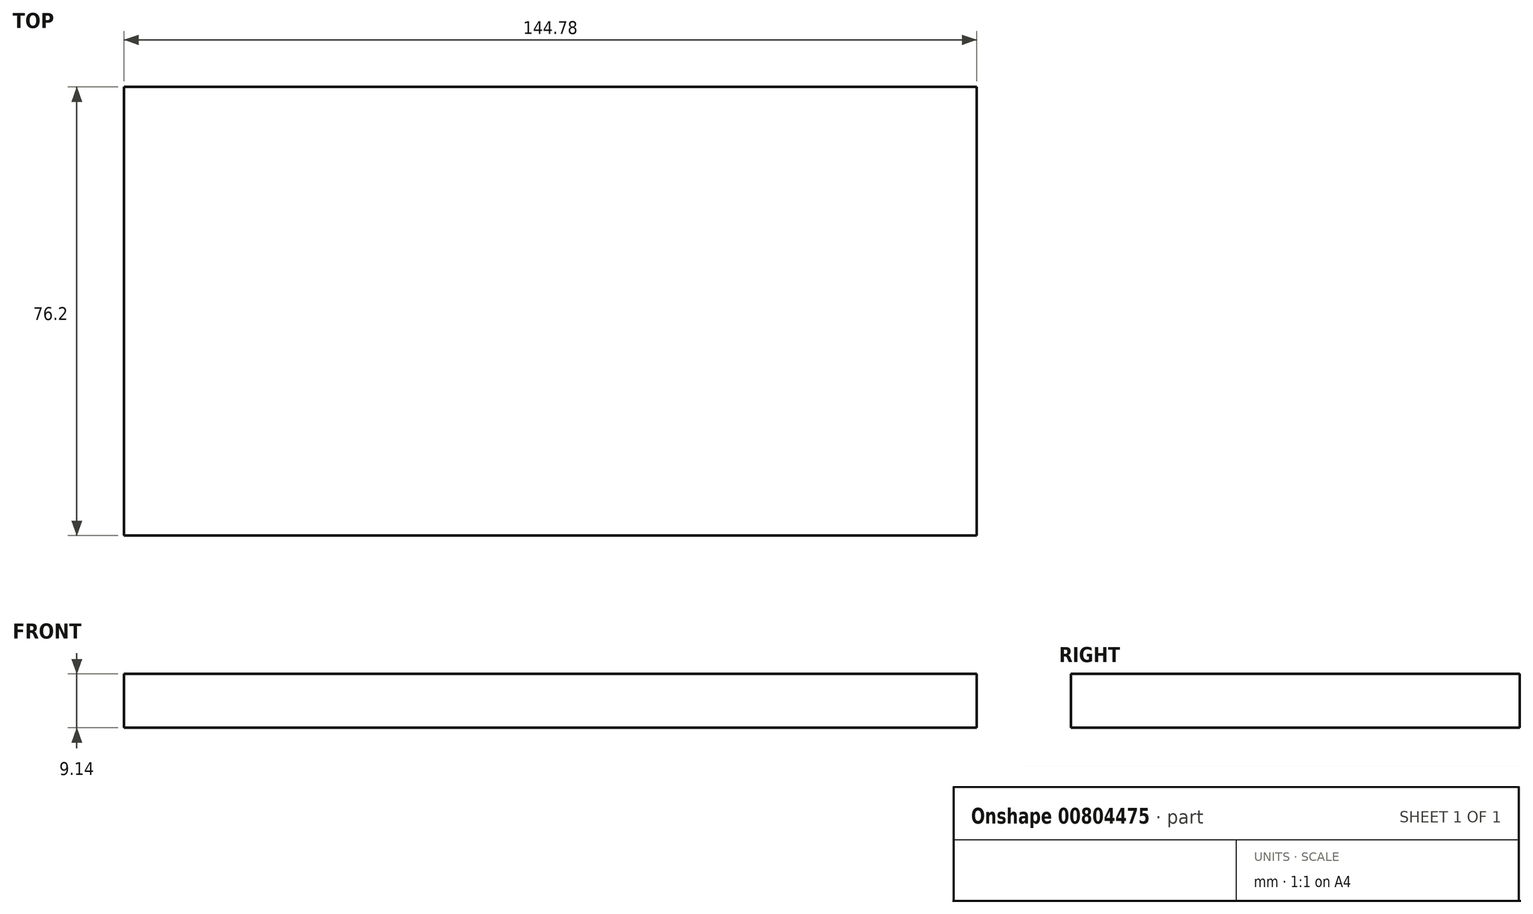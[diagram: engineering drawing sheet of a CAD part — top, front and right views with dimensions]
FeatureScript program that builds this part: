
annotation { "Feature Type Name" : "Feature", "Feature Type Description" : "" }
export const myFeature = defineFeature(function(context is Context, id is Id, definition is map)
    precondition{}
    {
        {
            var Q0;
            Q0=qCreatedBy(makeId("Top.planeOp"),FACE);
            var sketch = newSketch(context, id + "F0", { "sketchPlane" : qUnion([Q0])});
            skLineSegment(sketch, "E0.bottom", {"start": v(72.4, -38.1) * mm, "end": v(-72.4, -38.1) * mm});
            skLineSegment(sketch, "E0.top", {"start": v(72.4, 38.1) * mm, "end": v(-72.4, 38.1) * mm});
            skLineSegment(sketch, "E0.left", {"start": v(72.4, -38.1) * mm, "end": v(72.4, 38.1) * mm});
            skLineSegment(sketch, "E0.right", {"start": v(-72.4, -38.1) * mm, "end": v(-72.4, 38.1) * mm});
            skPoint(sketch, "E0.middle", {"position": v(0, 0) * mm});
            skSolve(sketch);
        }
        {
            var Q0;
            Q0=makeQuery(id+"F0.imprint","IMPRINT",FACE,{"disambiguationData":[TD([[makeQuery(id+"F0.imprint","IMPRINT",EDGE,{"derivedFrom":sQuery(id+"F0.wireOp",EDGE,"E0.bottom")}),-1.0]])]});
            extrude(context, id + "F1", {"entities" : qUnion([Q0]), "depth" : 9.14 * mm, "offsetDistance" : 25.4 * mm});
        }
    });
